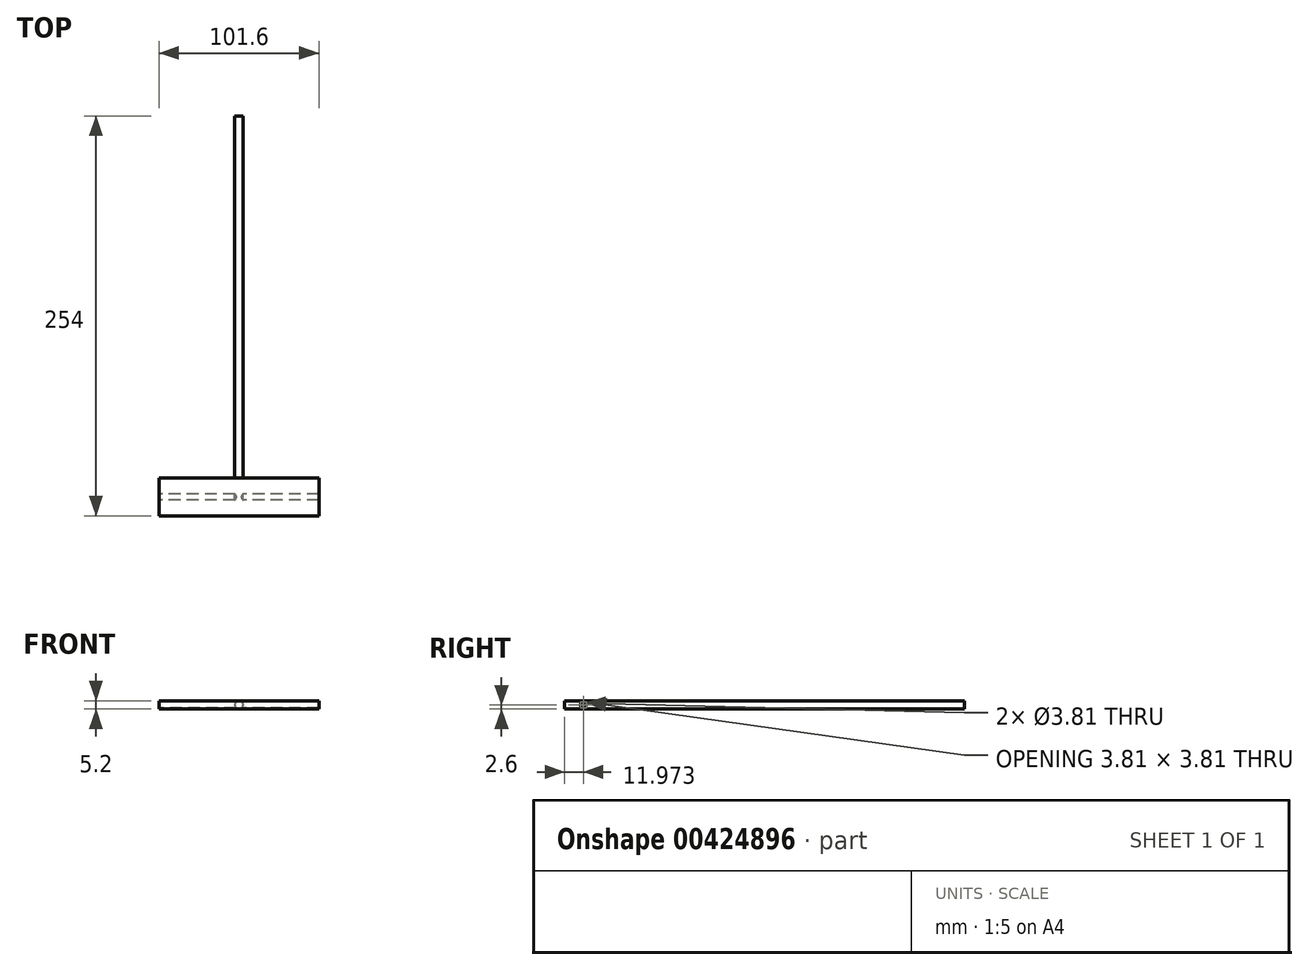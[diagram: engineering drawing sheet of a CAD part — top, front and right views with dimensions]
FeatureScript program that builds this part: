
annotation { "Feature Type Name" : "Feature", "Feature Type Description" : "" }
export const myFeature = defineFeature(function(context is Context, id is Id, definition is map)
    precondition{}
    {
        {
            var Q0;
            Q0=qCreatedBy(makeId("Front.planeOp"),FACE);
            var sketch = newSketch(context, id + "F0", { "sketchPlane" : qUnion([Q0])});
            skArc(sketch, "E0", {"start": v(0, 2.6) * mm, "mid": v(-2.6, 0) * mm, "end": v(0, -2.6) * mm});
            skLineSegment(sketch, "E1", {"start": v(0, 2.6) * mm, "end": v(0, -2.6) * mm});
            skSolve(sketch);
        }
        {
            var Q0;
            Q0 = qSketchRegion(id + "F0", true);
            extrude(context, id + "F1", {"entities" : qUnion([Q0]), "depth" : 127 * mm, "hasSecondDirection" : true, "secondDirectionOppositeDirection" : true, "secondDirectionDepth" : 127 * mm});
        }
        {
            var Q0;
            Q0=makeQuery(id+"F1.opExtrude","SWEPT_FACE",FACE,{"disambiguationData":[OSD([sQuery(id+"F0.wireOp",EDGE,"E1")])]});
            var sketch = newSketch(context, id + "F2", { "sketchPlane" : qUnion([Q0])});
            skLineSegment(sketch, "E2", {"start": v(-103.05, 2.6) * mm, "end": v(-103.05, -2.6) * mm});
            skLineSegment(sketch, "E3", {"start": v(-103.05, 0) * mm, "end": v(-127, 0) * mm});
            skCircle(sketch, "E4", {"center": v(-115.03, 0) * mm, "radius": 1.9 * mm});
            skSolve(sketch);
        }
        {
            var Q0;
            Q0=makeQuery(id+"F1.opExtrude","SWEPT_BODY",BODY,{"disambiguationData":[OSD([sQuery(id+"F0.wireOp",EDGE,"E0"),sQuery(id+"F0.wireOp",EDGE,"E1")])]});
            var Q1;
            Q1=qCreatedBy(makeId("Right.planeOp"),FACE);
            mirror(context, id + "F3", {"operationType" : NewBodyOperationType.ADD, "entities" : qUnion([Q0]), "mirrorPlane" : qUnion([Q1])});
        }
        {
            var Q0;
            {var subQ0=sQuery(id+"F2.wireOp",EDGE,"E4");var subQ1=sQuery(id+"F2.wireOp",EDGE,"E3");var subQ2=makeQuery(id+"F2.imprint","INTERSECT",VERTEX,{"disambiguationData":[OD(0.0)],"derivedFrom":[subQ1,subQ0]});Q0=makeQuery(id+"F2.imprint","IMPRINT",FACE,{"disambiguationData":[TD([[makeQuery(id+"F2.imprint","IMPRINT",EDGE,{"disambiguationData":[TD([[subQ2,-1.0]])],"derivedFrom":subQ1}),-1.0]])]});}
            var Q1;
            {var subQ0=sQuery(id+"F2.wireOp",EDGE,"E4");var subQ1=sQuery(id+"F2.wireOp",EDGE,"E3");var subQ2=makeQuery(id+"F2.imprint","INTERSECT",VERTEX,{"disambiguationData":[OD(0.0)],"derivedFrom":[subQ1,subQ0]});Q1=makeQuery(id+"F2.imprint","IMPRINT",FACE,{"disambiguationData":[TD([[makeQuery(id+"F2.imprint","IMPRINT",EDGE,{"disambiguationData":[TD([[subQ2,-1.0]])],"derivedFrom":subQ1}),1.0]])]});}
            extrude(context, id + "F4", {"entities" : qUnion([Q0, Q1]), "operationType" : NewBodyOperationType.ADD, "depth" : 50.8 * mm, "hasSecondDirection" : true, "secondDirectionOppositeDirection" : true, "secondDirectionDepth" : 50.8 * mm});
        }
    });
